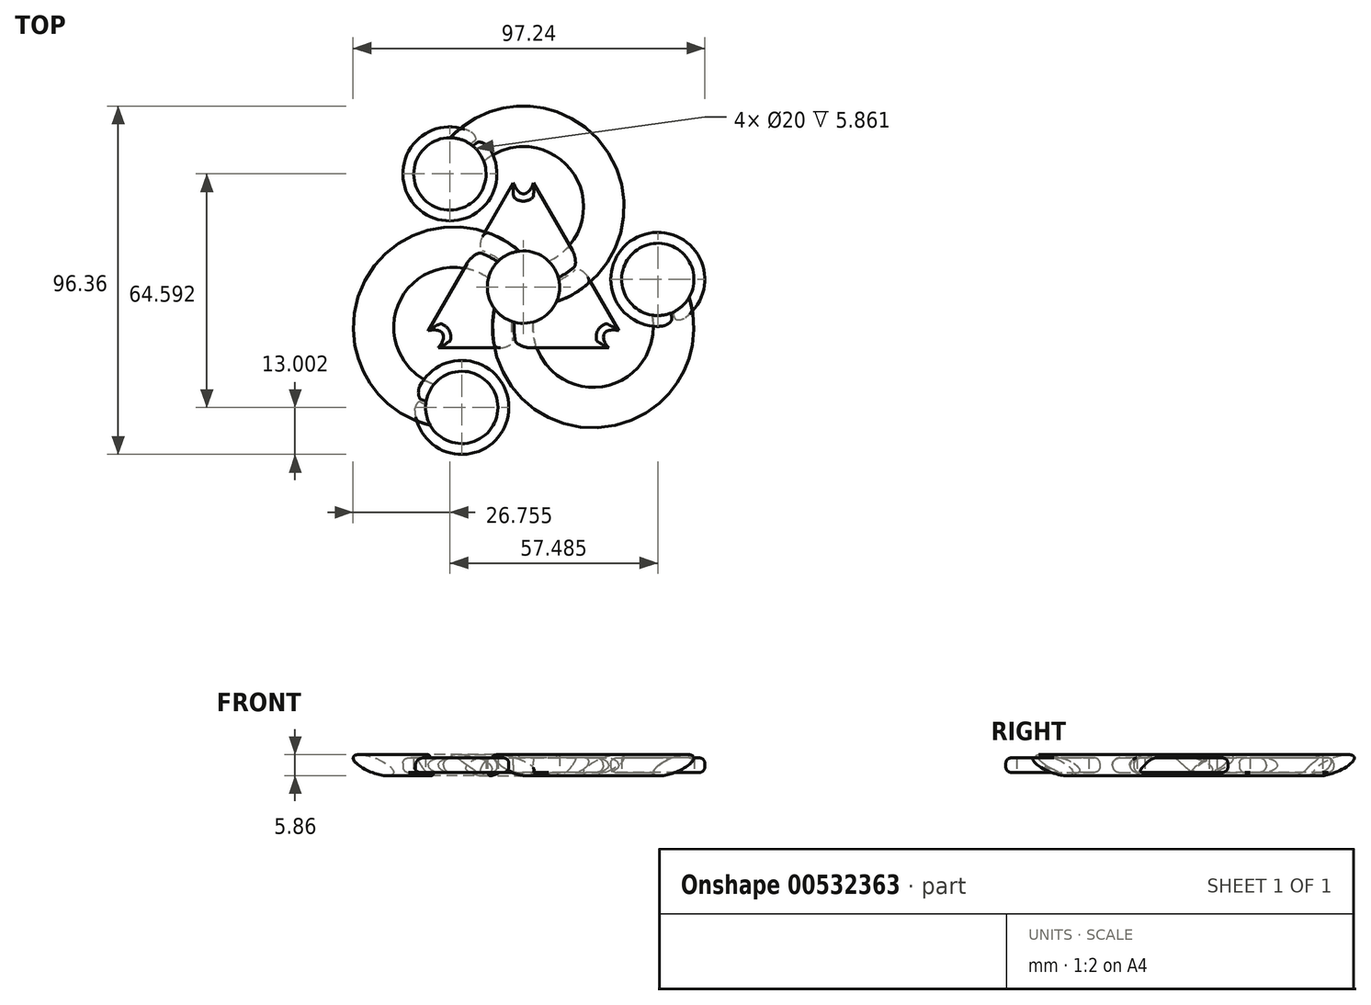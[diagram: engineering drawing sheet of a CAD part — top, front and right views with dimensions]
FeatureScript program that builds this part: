
annotation { "Feature Type Name" : "Feature", "Feature Type Description" : "" }
export const myFeature = defineFeature(function(context is Context, id is Id, definition is map)
    precondition{}
    {
        {
            var Q0;
            Q0=qCreatedBy(makeId("Top.planeOp"),FACE);
            var sketch = newSketch(context, id + "F0", { "sketchPlane" : qUnion([Q0])});
            skCircle(sketch, "E0", {"center": v(0, 0) * mm, "radius": 10 * mm});
            skArc(sketch, "E1", {"start": v(0, 0) * mm, "mid": v(18.62, 34.35) * mm, "end": v(-20.33, 31.31) * mm});
            skArc(sketch, "E2", {"start": v(0, 0) * mm, "mid": v(-39.04, -1) * mm, "end": v(-17.06, -33.28) * mm});
            skArc(sketch, "E3", {"start": v(0, 0) * mm, "mid": v(20.55, -33.3) * mm, "end": v(37.15, 2.14) * mm});
            skPoint(sketch, "E4", {"position": v(-20.33, 31.31) * mm});
            skPoint(sketch, "E5", {"position": v(-17.06, -33.28) * mm});
            skPoint(sketch, "E6", {"position": v(37.15, 2.14) * mm});
            skCircle(sketch, "E7", {"center": v(-20.33, 31.31) * mm, "radius": 10 * mm});
            skCircle(sketch, "E8", {"center": v(-17.06, -33.28) * mm, "radius": 10 * mm});
            skCircle(sketch, "E9", {"center": v(37.15, 2.14) * mm, "radius": 10 * mm});
            skCircle(sketch, "E10.0", {"center": v(-20.33, 31.31) * mm, "radius": 13 * mm});
            skCircle(sketch, "E11.0", {"center": v(-17.06, -33.28) * mm, "radius": 13 * mm});
            skCircle(sketch, "E12.0", {"center": v(37.15, 2.14) * mm, "radius": 13 * mm});
            skLineSegment(sketch, "E13", {"start": v(-29.88, -35.43) * mm, "end": v(-30.13, -30.54) * mm});
            skPoint(sketch, "E14.start.orphan", {"position": v(49.97, 0) * mm});
            skLineSegment(sketch, "E15.0", {"start": v(2.77, 28.82) * mm, "end": v(26.34, -12.02) * mm});
            skLineSegment(sketch, "E15.1", {"start": v(-26.34, -12.02) * mm, "end": v(-2.77, 28.82) * mm});
            skLineSegment(sketch, "E15.2", {"start": v(23.58, -16.8) * mm, "end": v(-23.58, -16.8) * mm});
            skEllipticalArc(sketch, "E16", {});
            skEllipticalArc(sketch, "E17", {});
            skEllipticalArc(sketch, "E18", {});
            const initialGuessF0  = {"E16": [0, 0.033611037137291105, 0, -1, 0.007827405186674269, 0.003496816581027269, 5.37093435019608, 0.9122509569835051], "E17": [0.029108012008436292, -0.01680551856864554, 0.8660254037844386, -0.5, 0.007827405186674269, 0.003496816581027269, 2.229341696606287, 4.053843610573301], "E18": [-0.02910801200843629, -0.016805518568645567, -0.8660254037844386, -0.5, 0.007827405186674269, 0.003496816581027269, 2.229341696606287, 4.053843610573299]};
            skSetInitialGuess(sketch, initialGuessF0);
            skSolve(sketch);
        }
        {
            var Q0;
            Q0=sQuery(id+"F0.wireOp",VERTEX,"E1.end");
            var Q1;
            Q1=sQuery(id+"F0.wireOp",EDGE,"E1");
            cPlane(context, id + "F1", {"entities" : qUnion([Q0, Q1]), "cplaneType" : CPlaneType.CURVE_POINT, "offset" : 25 * mm, "width" : 150 * mm, "height" : 150 * mm});
        }
        {
            var Q0;
            Q0=sQuery(id+"F0.wireOp",VERTEX,"E2.end");
            var Q1;
            Q1=sQuery(id+"F0.wireOp",EDGE,"E2");
            cPlane(context, id + "F2", {"entities" : qUnion([Q0, Q1]), "cplaneType" : CPlaneType.CURVE_POINT, "offset" : 25 * mm, "width" : 150 * mm, "height" : 150 * mm});
        }
        {
            var Q0;
            Q0=sQuery(id+"F0.wireOp",VERTEX,"E3.end");
            var Q1;
            Q1=sQuery(id+"F0.wireOp",EDGE,"E3");
            cPlane(context, id + "F3", {"entities" : qUnion([Q0, Q1]), "cplaneType" : CPlaneType.CURVE_POINT, "offset" : 25 * mm, "width" : 150 * mm, "height" : 150 * mm});
        }
        {
            var Q0;
            Q0=qCreatedBy(id+"F1.planeOp",FACE);
            var sketch = newSketch(context, id + "F4", { "sketchPlane" : qUnion([Q0])});
            skEllipse(sketch, "E19", {"center": v(-31.34, 0) * mm, "majorRadius": 6 * mm, "minorRadius": 2 * mm, "majorAxis": v(-0.93, 0.38)});
            skSolve(sketch);
        }
        {
            var Q0;
            Q0=qCreatedBy(id+"F2.planeOp",FACE);
            var sketch = newSketch(context, id + "F5", { "sketchPlane" : qUnion([Q0])});
            skEllipse(sketch, "E20", {"center": v(-31.44, 0) * mm, "majorRadius": 6 * mm, "minorRadius": 2 * mm, "majorAxis": v(-0.93, 0.38)});
            skSolve(sketch);
        }
        {
            var Q0;
            Q0=qCreatedBy(id+"F3.planeOp",FACE);
            var sketch = newSketch(context, id + "F6", { "sketchPlane" : qUnion([Q0])});
            skEllipse(sketch, "E21", {"center": v(-31.13, 0) * mm, "majorRadius": 6 * mm, "minorRadius": 2 * mm, "majorAxis": v(-0.93, 0.38)});
            skSolve(sketch);
        }
        {
            var Q0;
            Q0=makeQuery(id+"F5.imprint","IMPRINT",FACE,{"disambiguationData":[TD([[makeQuery(id+"F5.imprint","IMPRINT",EDGE,{"derivedFrom":sQuery(id+"F5.wireOp",EDGE,"E20")}),1.0]])]});
            var Q1;
            Q1=sQuery(id+"F0.wireOp",EDGE,"E2");
            sweep(context, id + "F7", {"profiles" : qUnion([Q0]), "path" : qUnion([Q1])});
        }
        {
            var Q0;
            Q0=makeQuery(id+"F4.imprint","IMPRINT",FACE,{"disambiguationData":[TD([[makeQuery(id+"F4.imprint","IMPRINT",EDGE,{"derivedFrom":sQuery(id+"F4.wireOp",EDGE,"E19")}),1.0]])]});
            var Q1;
            Q1=sQuery(id+"F0.wireOp",EDGE,"E1");
            sweep(context, id + "F8", {"operationType" : NewBodyOperationType.ADD, "profiles" : qUnion([Q0]), "path" : qUnion([Q1])});
        }
        {
            var Q0;
            Q0=makeQuery(id+"F6.imprint","IMPRINT",FACE,{"disambiguationData":[TD([[makeQuery(id+"F6.imprint","IMPRINT",EDGE,{"derivedFrom":sQuery(id+"F6.wireOp",EDGE,"E21")}),1.0]])]});
            var Q1;
            Q1=sQuery(id+"F0.wireOp",EDGE,"E3");
            sweep(context, id + "F9", {"operationType" : NewBodyOperationType.ADD, "profiles" : qUnion([Q0]), "path" : qUnion([Q1])});
        }
        {
            var Q0;
            {var subQ0=sQuery(id+"F0.wireOp",EDGE,"E2");var subQ3=sQuery(id+"F0.wireOp",EDGE,"E0");var subQ4=makeQuery(id+"F0.imprint","INTERSECT",VERTEX,{"derivedFrom":[subQ3,subQ0]});Q0=makeQuery(id+"F0.imprint","IMPRINT",FACE,{"disambiguationData":[TD([[makeQuery(id+"F0.imprint","IMPRINT",EDGE,{"disambiguationData":[TD([[subQ4,-1.0]])],"derivedFrom":subQ3}),-1.0]])]});}
            var Q1;
            {var subQ0=sQuery(id+"F0.wireOp",EDGE,"E1");var subQ3=sQuery(id+"F0.wireOp",EDGE,"E0");var subQ4=makeQuery(id+"F0.imprint","INTERSECT",VERTEX,{"derivedFrom":[subQ3,subQ0]});Q1=makeQuery(id+"F0.imprint","IMPRINT",FACE,{"disambiguationData":[TD([[makeQuery(id+"F0.imprint","IMPRINT",EDGE,{"disambiguationData":[TD([[subQ4,1.0]])],"derivedFrom":subQ3}),-1.0]])]});}
            var Q2;
            {var subQ3=sQuery(id+"F0.wireOp",EDGE,"E2");var subQ7=sQuery(id+"F0.wireOp",EDGE,"E0");var subQ9=makeQuery(id+"F0.imprint","INTERSECT",VERTEX,{"derivedFrom":[subQ7,subQ3]});Q2=makeQuery(id+"F0.imprint","IMPRINT",FACE,{"disambiguationData":[TD([[makeQuery(id+"F0.imprint","IMPRINT",EDGE,{"disambiguationData":[TD([[subQ9,1.0]])],"derivedFrom":subQ7}),-1.0]])]});}
            extrude(context, id + "F10", {"entities" : qUnion([Q0, Q1, Q2]), "operationType" : NewBodyOperationType.ADD, "endBound" : BoundingType.SYMMETRIC, "depth" : 4 * mm, "offsetDistance" : 25 * mm});
        }
        {
            var Q0;
            {var subQ0=sQuery(id+"F0.wireOp",EDGE,"E1");var subQ1=sQuery(id+"F0.wireOp",EDGE,"E0");var subQ2=makeQuery(id+"F0.imprint","INTERSECT",VERTEX,{"derivedFrom":[subQ1,subQ0]});Q0=makeQuery(id+"F0.imprint","IMPRINT",FACE,{"disambiguationData":[TD([[makeQuery(id+"F0.imprint","IMPRINT",EDGE,{"disambiguationData":[TD([[subQ2,1.0]])],"derivedFrom":subQ1}),1.0]])]});}
            var Q1;
            {var subQ0=sQuery(id+"F0.wireOp",EDGE,"E2");var subQ1=sQuery(id+"F0.wireOp",EDGE,"E0");var subQ2=makeQuery(id+"F0.imprint","INTERSECT",VERTEX,{"derivedFrom":[subQ1,subQ0]});Q1=makeQuery(id+"F0.imprint","IMPRINT",FACE,{"disambiguationData":[TD([[makeQuery(id+"F0.imprint","IMPRINT",EDGE,{"disambiguationData":[TD([[subQ2,-1.0]])],"derivedFrom":subQ1}),1.0]])]});}
            var Q2;
            {var subQ0=sQuery(id+"F0.wireOp",EDGE,"E2");var subQ1=sQuery(id+"F0.wireOp",EDGE,"E0");var subQ2=makeQuery(id+"F0.imprint","INTERSECT",VERTEX,{"derivedFrom":[subQ1,subQ0]});Q2=makeQuery(id+"F0.imprint","IMPRINT",FACE,{"disambiguationData":[TD([[makeQuery(id+"F0.imprint","IMPRINT",EDGE,{"disambiguationData":[TD([[subQ2,1.0]])],"derivedFrom":subQ1}),1.0]])]});}
            var Q3;
            Q3=sQuery(id+"F0.wireOp",EDGE,"E0");
            extrude(context, id + "F11", {"entities" : qUnion([Q0, Q1, Q2]), "operationType" : NewBodyOperationType.REMOVE, "surfaceEntities" : qUnion([Q3]), "endBound" : BoundingType.SYMMETRIC, "oppositeDirection" : true, "depth" : 17.6 * mm, "offsetDistance" : 25 * mm});
        }
        {
            var Q0;
            Q0=makeQuery(id+"F0.imprint","IMPRINT",FACE,{"disambiguationData":[TD([[makeQuery(id+"F0.imprint","IMPRINT",EDGE,{"derivedFrom":sQuery(id+"F0.wireOp",EDGE,"E8")}),-1.0]])]});
            var Q1;
            Q1=makeQuery(id+"F0.imprint","IMPRINT",FACE,{"disambiguationData":[TD([[makeQuery(id+"F0.imprint","IMPRINT",EDGE,{"derivedFrom":sQuery(id+"F0.wireOp",EDGE,"E7")}),-1.0]])]});
            var Q2;
            Q2=makeQuery(id+"F0.imprint","IMPRINT",FACE,{"disambiguationData":[TD([[makeQuery(id+"F0.imprint","IMPRINT",EDGE,{"derivedFrom":sQuery(id+"F0.wireOp",EDGE,"E9")}),-1.0]])]});
            extrude(context, id + "F12", {"entities" : qUnion([Q0, Q1, Q2]), "operationType" : NewBodyOperationType.ADD, "endBound" : BoundingType.SYMMETRIC, "depth" : 4 * mm, "offsetDistance" : 25 * mm});
        }
        {
            var Q0;
            Q0=makeQuery(id+"F0.imprint","IMPRINT",FACE,{"disambiguationData":[TD([[makeQuery(id+"F0.imprint","IMPRINT",EDGE,{"derivedFrom":sQuery(id+"F0.wireOp",EDGE,"E7")}),1.0]])]});
            extrude(context, id + "F13", {"entities" : qUnion([Q0]), "operationType" : NewBodyOperationType.REMOVE, "endBound" : BoundingType.SYMMETRIC, "oppositeDirection" : true, "depth" : 10 * mm, "offsetDistance" : 25 * mm});
        }
        {
            var Q0;
            Q0=makeQuery(id+"F0.imprint","IMPRINT",FACE,{"disambiguationData":[TD([[makeQuery(id+"F0.imprint","IMPRINT",EDGE,{"derivedFrom":sQuery(id+"F0.wireOp",EDGE,"E8")}),1.0]])]});
            extrude(context, id + "F14", {"entities" : qUnion([Q0]), "operationType" : NewBodyOperationType.REMOVE, "endBound" : BoundingType.SYMMETRIC, "oppositeDirection" : true, "depth" : 10 * mm, "offsetDistance" : 25 * mm});
        }
        {
            var Q0;
            Q0=makeQuery(id+"F0.imprint","IMPRINT",FACE,{"disambiguationData":[TD([[makeQuery(id+"F0.imprint","IMPRINT",EDGE,{"derivedFrom":sQuery(id+"F0.wireOp",EDGE,"E9")}),1.0]])]});
            extrude(context, id + "F15", {"entities" : qUnion([Q0]), "operationType" : NewBodyOperationType.REMOVE, "endBound" : BoundingType.SYMMETRIC, "depth" : 10 * mm, "offsetDistance" : 25 * mm});
        }
        {
            var Q0;
            {var subQ0=sQuery(id+"F0.wireOp",EDGE,"E18");var subQ1=sQuery(id+"F0.wireOp",EDGE,"E15.1");Q0=makeQuery(id+"F10.boolean.opBoolean","SPLIT",EDGE,{"disambiguationData":[TD([makeQuery(id+"F10.opExtrude","SWEPT_FACE",FACE,{"disambiguationData":[OSD([subQ0])]})])],"derivedFrom":makeQuery(id+"F10.opExtrude","CAP_EDGE",EDGE,{"disambiguationData":[OSD([subQ1])],"isStart":true})});}
            var Q1;
            Q1=makeQuery(id+"F10.opExtrude","CAP_EDGE",EDGE,{"disambiguationData":[OSD([sQuery(id+"F0.wireOp",EDGE,"E18")])],"isStart":true});
            var Q2;
            {var subQ0=sQuery(id+"F0.wireOp",EDGE,"E15.2");var subQ1=sQuery(id+"F0.wireOp",EDGE,"E18");Q2=makeQuery(id+"F10.boolean.opBoolean","SPLIT",EDGE,{"disambiguationData":[TD([makeQuery(id+"F10.opExtrude","SWEPT_FACE",FACE,{"disambiguationData":[OSD([subQ1])]})])],"derivedFrom":makeQuery(id+"F10.opExtrude","CAP_EDGE",EDGE,{"disambiguationData":[OSD([subQ0])],"isStart":true})});}
            var Q3;
            {var subQ0=sQuery(id+"F0.wireOp",EDGE,"E15.2");var subQ1=sQuery(id+"F0.wireOp",EDGE,"E17");Q3=makeQuery(id+"F10.boolean.opBoolean","SPLIT",EDGE,{"disambiguationData":[TD([makeQuery(id+"F10.opExtrude","SWEPT_FACE",FACE,{"disambiguationData":[OSD([subQ1])]})])],"derivedFrom":makeQuery(id+"F10.opExtrude","CAP_EDGE",EDGE,{"disambiguationData":[OSD([subQ0])],"isStart":true})});}
            var Q4;
            Q4=makeQuery(id+"F10.opExtrude","CAP_EDGE",EDGE,{"disambiguationData":[OSD([sQuery(id+"F0.wireOp",EDGE,"E17")])],"isStart":true});
            var Q5;
            {var subQ0=sQuery(id+"F0.wireOp",EDGE,"E15.0");var subQ1=sQuery(id+"F0.wireOp",EDGE,"E17");Q5=makeQuery(id+"F10.boolean.opBoolean","SPLIT",EDGE,{"disambiguationData":[TD([makeQuery(id+"F10.opExtrude","SWEPT_FACE",FACE,{"disambiguationData":[OSD([subQ1])]})])],"derivedFrom":makeQuery(id+"F10.opExtrude","CAP_EDGE",EDGE,{"disambiguationData":[OSD([subQ0])],"isStart":true})});}
            var Q6;
            {var subQ0=sQuery(id+"F0.wireOp",EDGE,"E15.0");var subQ1=sQuery(id+"F0.wireOp",EDGE,"E16");Q6=makeQuery(id+"F10.boolean.opBoolean","SPLIT",EDGE,{"disambiguationData":[TD([makeQuery(id+"F10.opExtrude","SWEPT_FACE",FACE,{"disambiguationData":[OSD([subQ1])]})])],"derivedFrom":makeQuery(id+"F10.opExtrude","CAP_EDGE",EDGE,{"disambiguationData":[OSD([subQ0])],"isStart":true})});}
            var Q7;
            Q7=makeQuery(id+"F10.opExtrude","CAP_EDGE",EDGE,{"disambiguationData":[OSD([sQuery(id+"F0.wireOp",EDGE,"E16")])],"isStart":true});
            var Q8;
            {var subQ0=sQuery(id+"F0.wireOp",EDGE,"E16");var subQ1=sQuery(id+"F0.wireOp",EDGE,"E15.1");Q8=makeQuery(id+"F10.boolean.opBoolean","SPLIT",EDGE,{"disambiguationData":[TD([makeQuery(id+"F10.opExtrude","SWEPT_FACE",FACE,{"disambiguationData":[OSD([subQ0])]})])],"derivedFrom":makeQuery(id+"F10.opExtrude","CAP_EDGE",EDGE,{"disambiguationData":[OSD([subQ1])],"isStart":true})});}
            var Q9;
            {var subQ0=sQuery(id+"F0.wireOp",EDGE,"E15.0");var subQ1=sQuery(id+"F0.wireOp",EDGE,"E16");Q9=makeQuery(id+"F10.boolean.opBoolean","SPLIT",EDGE,{"disambiguationData":[TD([makeQuery(id+"F10.opExtrude","SWEPT_FACE",FACE,{"disambiguationData":[OSD([subQ1])]})])],"derivedFrom":makeQuery(id+"F10.opExtrude","CAP_EDGE",EDGE,{"disambiguationData":[OSD([subQ0])],"isStart":false})});}
            var Q10;
            Q10=makeQuery(id+"F10.opExtrude","CAP_EDGE",EDGE,{"disambiguationData":[OSD([sQuery(id+"F0.wireOp",EDGE,"E16")])],"isStart":false});
            var Q11;
            {var subQ0=sQuery(id+"F0.wireOp",EDGE,"E16");var subQ1=sQuery(id+"F0.wireOp",EDGE,"E15.1");Q11=makeQuery(id+"F10.boolean.opBoolean","SPLIT",EDGE,{"disambiguationData":[TD([makeQuery(id+"F10.opExtrude","SWEPT_FACE",FACE,{"disambiguationData":[OSD([subQ0])]})])],"derivedFrom":makeQuery(id+"F10.opExtrude","CAP_EDGE",EDGE,{"disambiguationData":[OSD([subQ1])],"isStart":false})});}
            var Q12;
            {var subQ0=sQuery(id+"F0.wireOp",EDGE,"E18");var subQ1=sQuery(id+"F0.wireOp",EDGE,"E15.1");Q12=makeQuery(id+"F10.boolean.opBoolean","SPLIT",EDGE,{"disambiguationData":[TD([makeQuery(id+"F10.opExtrude","SWEPT_FACE",FACE,{"disambiguationData":[OSD([subQ0])]})])],"derivedFrom":makeQuery(id+"F10.opExtrude","CAP_EDGE",EDGE,{"disambiguationData":[OSD([subQ1])],"isStart":false})});}
            var Q13;
            Q13=makeQuery(id+"F10.opExtrude","CAP_EDGE",EDGE,{"disambiguationData":[OSD([sQuery(id+"F0.wireOp",EDGE,"E18")])],"isStart":false});
            var Q14;
            {var subQ0=sQuery(id+"F0.wireOp",EDGE,"E15.2");var subQ1=sQuery(id+"F0.wireOp",EDGE,"E18");Q14=makeQuery(id+"F10.boolean.opBoolean","SPLIT",EDGE,{"disambiguationData":[TD([makeQuery(id+"F10.opExtrude","SWEPT_FACE",FACE,{"disambiguationData":[OSD([subQ1])]})])],"derivedFrom":makeQuery(id+"F10.opExtrude","CAP_EDGE",EDGE,{"disambiguationData":[OSD([subQ0])],"isStart":false})});}
            var Q15;
            {var subQ0=sQuery(id+"F0.wireOp",EDGE,"E15.2");var subQ1=sQuery(id+"F0.wireOp",EDGE,"E17");Q15=makeQuery(id+"F10.boolean.opBoolean","SPLIT",EDGE,{"disambiguationData":[TD([makeQuery(id+"F10.opExtrude","SWEPT_FACE",FACE,{"disambiguationData":[OSD([subQ1])]})])],"derivedFrom":makeQuery(id+"F10.opExtrude","CAP_EDGE",EDGE,{"disambiguationData":[OSD([subQ0])],"isStart":false})});}
            var Q16;
            Q16=makeQuery(id+"F10.opExtrude","CAP_EDGE",EDGE,{"disambiguationData":[OSD([sQuery(id+"F0.wireOp",EDGE,"E17")])],"isStart":false});
            var Q17;
            {var subQ0=sQuery(id+"F0.wireOp",EDGE,"E15.0");var subQ1=sQuery(id+"F0.wireOp",EDGE,"E17");Q17=makeQuery(id+"F10.boolean.opBoolean","SPLIT",EDGE,{"disambiguationData":[TD([makeQuery(id+"F10.opExtrude","SWEPT_FACE",FACE,{"disambiguationData":[OSD([subQ1])]})])],"derivedFrom":makeQuery(id+"F10.opExtrude","CAP_EDGE",EDGE,{"disambiguationData":[OSD([subQ0])],"isStart":false})});}
            fillet(context, id + "F16", {"entities" : qUnion([Q0, Q1, Q2, Q3, Q4, Q5, Q6, Q7, Q8, Q9, Q10, Q11, Q12, Q13, Q14, Q15, Q16, Q17]), "radius" : 2 * mm, "tangentPropagation" : true, "allowEdgeOverflow" : false});
        }
        {
            var Q0;
            Q0=makeQuery(id+"F12.opExtrude","CAP_EDGE",EDGE,{"disambiguationData":[OSD([sQuery(id+"F0.wireOp",EDGE,"E12.0")])],"isStart":false});
            var Q1;
            Q1=makeQuery(id+"F12.opExtrude","CAP_EDGE",EDGE,{"disambiguationData":[OSD([sQuery(id+"F0.wireOp",EDGE,"E10.0")])],"isStart":false});
            var Q2;
            Q2=makeQuery(id+"F12.opExtrude","CAP_EDGE",EDGE,{"disambiguationData":[OSD([sQuery(id+"F0.wireOp",EDGE,"E11.0")])],"isStart":false});
            var Q3;
            Q3=makeQuery(id+"F12.boolean.opBoolean","SPLIT",EDGE,{"disambiguationData":[OD(0.0)],"derivedFrom":makeQuery(id+"F12.opExtrude","CAP_EDGE",EDGE,{"disambiguationData":[OSD([sQuery(id+"F0.wireOp",EDGE,"E11.0")])],"isStart":true})});
            var Q4;
            Q4=makeQuery(id+"F12.opExtrude","CAP_EDGE",EDGE,{"disambiguationData":[OSD([sQuery(id+"F0.wireOp",EDGE,"E12.0")])],"isStart":true});
            var Q5;
            Q5=makeQuery(id+"F12.opExtrude","CAP_EDGE",EDGE,{"disambiguationData":[OSD([sQuery(id+"F0.wireOp",EDGE,"E10.0")])],"isStart":true});
            fillet(context, id + "F17", {"entities" : qUnion([Q0, Q1, Q2, Q3, Q4, Q5]), "radius" : 1.5 * mm, "allowEdgeOverflow" : false});
        }
    });
